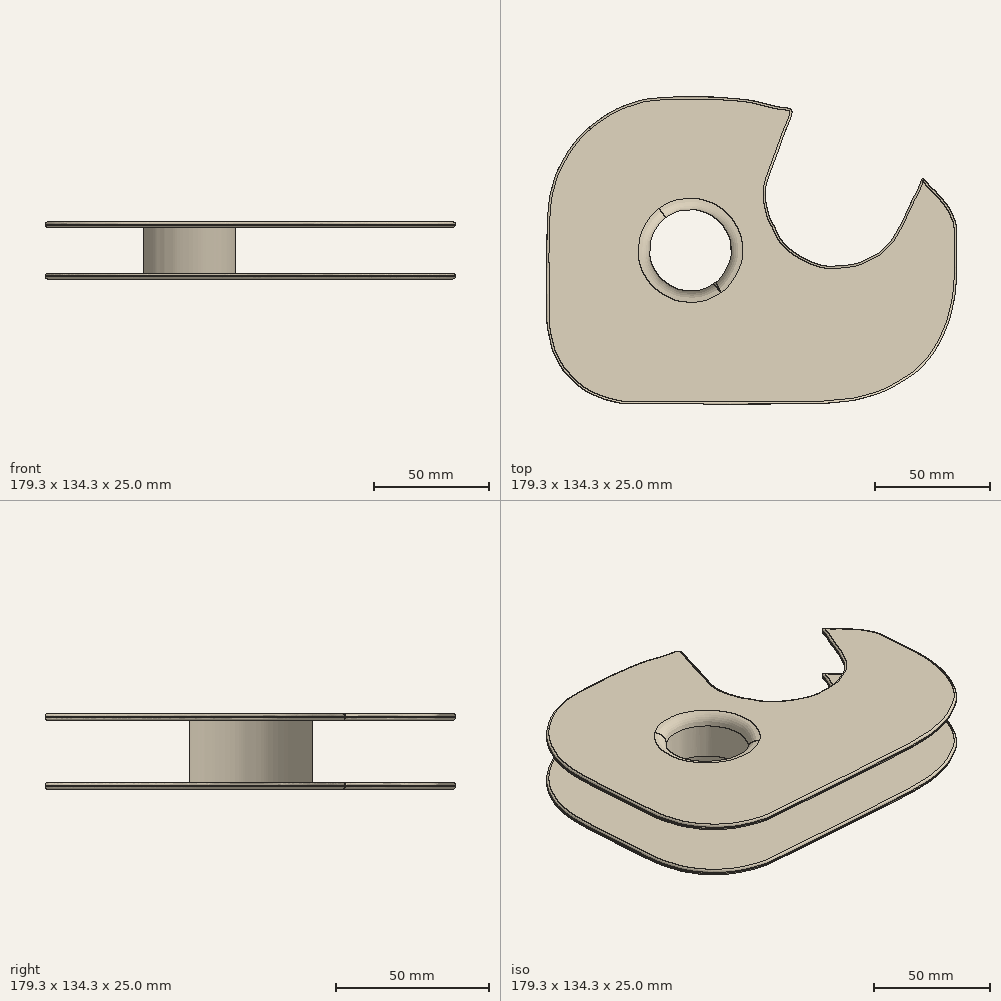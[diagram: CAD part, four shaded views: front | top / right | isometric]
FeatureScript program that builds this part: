
annotation { "Feature Type Name" : "Feature", "Feature Type Description" : "" }
export const myFeature = defineFeature(function(context is Context, id is Id, definition is map)
    precondition{}
    {
        {
            var Q0;
            Q0=qCreatedBy(makeId("Top.planeOp"),FACE);
            var sketch = newSketch(context, id + "F0", { "sketchPlane" : qUnion([Q0])});
            skFitSpline(sketch, "E0", {"points": [v(111.73, 142.36) * mm, v(107.12, 143.84) * mm, v(98.6, 145.82) * mm, v(92.37, 147.1) * mm, v(85.57, 147.8) * mm, v(81.03, 148.1) * mm, v(76.77, 148.37) * mm, v(69.4, 148.37) * mm, v(61.32, 148.37) * mm, v(54.94, 148.1) * mm, v(51.73, 147.73) * mm, v(47.4, 147.28) * mm, v(43.51, 146.14) * mm, v(37.8, 144.2) * mm, v(32.1, 141.34) * mm, v(27.3, 138.14) * mm, v(20.34, 132.32) * mm, v(14.28, 124.9) * mm, v(12, 121.02) * mm, v(8.92, 115.08) * mm, v(7.1, 109.37) * mm, v(5.72, 103.43) * mm, v(5.26, 98.87) * mm, v(4.92, 94.87) * mm, v(4.7, 49.9) * mm, v(4.98, 47.88) * mm, v(5.34, 45.12) * mm, v(6.17, 42) * mm, v(6.63, 39.6) * mm, v(7.55, 36.66) * mm, v(8.7, 34.2) * mm, v(10.18, 31.6) * mm, v(11.5, 29.24) * mm, v(13.73, 26.87) * mm, v(15.5, 24.8) * mm, v(17.28, 23.17) * mm, v(19.36, 21.4) * mm, v(21.28, 20.06) * mm, v(23.65, 18.73) * mm, v(26.76, 17.4) * mm, v(29.57, 16.28) * mm, v(33.28, 15.25) * mm, v(36.68, 14.5) * mm, v(40.38, 14.28) * mm, v(121.15, 14.2) * mm, v(129.89, 14.65) * mm, v(134.18, 15.1) * mm, v(138.92, 15.69) * mm, v(144.99, 17.17) * mm, v(151.2, 19.19) * mm, v(155.79, 21.3) * mm, v(161.76, 24.89) * mm, v(166.55, 28.2) * mm, v(172.43, 34.45) * mm, v(175.65, 39.41) * mm, v(178.22, 44.47) * mm, v(180.43, 49.99) * mm, v(181.53, 53.94) * mm, v(183, 60.84) * mm, v(183.55, 66.08) * mm, v(183.74, 68.65) * mm, v(183.74, 72.14) * mm, v(183.74, 89.98) * mm, v(183.1, 94.3) * mm, v(181.62, 97.61) * mm, v(179.6, 101.2) * mm, v(176.1, 105.33) * mm, v(174.08, 107.54) * mm, v(171.79, 109.75) * mm, v(169.12, 112.5) * mm, v(168.02, 110.67) * mm, v(165.81, 105.7) * mm, v(164.52, 103.5) * mm, v(163.24, 100.46) * mm, v(161.03, 95.77) * mm, v(159.56, 92.65) * mm, v(157.35, 88.97) * mm, v(155.24, 85.38) * mm, v(153.67, 83.82) * mm, v(150.18, 80.33) * mm, v(146.41, 78.4) * mm, v(141.9, 76.1) * mm, v(138.6, 75.18) * mm, v(134.55, 74.63) * mm, v(131.24, 74.44) * mm, v(126.83, 74.44) * mm, v(121.68, 75.73) * mm, v(115.8, 78.49) * mm, v(111.02, 81.8) * mm, v(106.51, 86.76) * mm, v(103.94, 92.1) * mm, v(102.65, 94.3) * mm, v(100.53, 102.02) * mm, v(100.44, 109.01) * mm, v(103.57, 118.57) * mm, v(107.25, 128.32) * mm, v(109.08, 133.65) * mm, v(111.73, 142.36) * mm]});
            skFitSpline(sketch, "E1", {"points": [v(49.78, 78.39) * mm, v(50.73, 74.81) * mm, v(52.22, 72.07) * mm, v(53.65, 70.04) * mm, v(54.85, 68.73) * mm, v(56.34, 67.66) * mm, v(58, 66.35) * mm, v(59.67, 65.51) * mm, v(61.82, 64.44) * mm, v(65.52, 63.72) * mm, v(69.33, 63.6) * mm, v(73.03, 64.26) * mm, v(75.41, 65.4) * mm, v(77.2, 66.35) * mm, v(78.15, 67.06) * mm, v(79.47, 67.78) * mm, v(80.3, 68.8) * mm, v(81.61, 70.46) * mm, v(82.75, 72.3) * mm, v(83.76, 74.28) * mm, v(85.07, 77.85) * mm, v(85.25, 80.65) * mm, v(85.13, 83.58) * mm, v(84.65, 86.26) * mm, v(83.22, 89.48) * mm, v(82.39, 90.85) * mm, v(81.08, 92.82) * mm, v(79.17, 94.66) * mm, v(76.84, 96.4) * mm, v(74.64, 97.52) * mm, v(70.7, 98.84) * mm, v(67.48, 98.96) * mm, v(63.31, 98.6) * mm, v(60.63, 97.76) * mm, v(57.11, 95.74) * mm, v(54.6, 93.53) * mm, v(52.34, 90.43) * mm, v(51.15, 88.28) * mm, v(50.14, 85.18) * mm, v(49.84, 82.14) * mm, v(49.78, 78.39) * mm]});
            skSolve(sketch);
        }
        {
            var Q0;
            Q0 = qSketchRegion(id + "F0", true);
            extrude(context, id + "F1", {"entities" : qUnion([Q0]), "depth" : 25 * mm});
        }
        {
            var Q0;
            Q0=makeQuery(id+"F1.opExtrude","SWEPT_FACE",FACE,{"disambiguationData":[OSD([sQuery(id+"F0.wireOp",EDGE,"E0")])]});
            shell(context, id + "F2", {"entities" : qUnion([Q0]), "thickness" : 2.5 * mm});
        }
        {
            var Q0;
            Q0=makeQuery(id+"F1.opExtrude","CAP_EDGE",EDGE,{"disambiguationData":[OSD([sQuery(id+"F0.wireOp",EDGE,"E1")])],"isStart":false});
            var Q1;
            Q1=makeQuery(id+"F1.opExtrude","CAP_EDGE",EDGE,{"disambiguationData":[OSD([sQuery(id+"F0.wireOp",EDGE,"E1")])],"isStart":true});
            fillet(context, id + "F3", {"entities" : qUnion([Q0, Q1]), "radius" : 5 * mm, "tangentPropagation" : true, "allowEdgeOverflow" : false});
        }
        {
            var Q0;
            Q0=makeQuery(id+"F1.opExtrude","CAP_EDGE",EDGE,{"disambiguationData":[OSD([sQuery(id+"F0.wireOp",EDGE,"E0")])],"isStart":false});
            var Q1;
            {var subQ0=sQuery(id+"F0.wireOp",EDGE,"E0");Q1=makeQuery(id+"F2.opShell","OFFSET_EDGE",EDGE,{"disambiguationData":[OSD([subQ0]),TDD([makeQuery(id+"F1.opExtrude","CAP_EDGE",EDGE,{"disambiguationData":[OSD([subQ0])],"isStart":false})])]});}
            var Q2;
            {var subQ0=sQuery(id+"F0.wireOp",EDGE,"E0");Q2=makeQuery(id+"F2.opShell","OFFSET_EDGE",EDGE,{"disambiguationData":[OSD([subQ0]),TDD([makeQuery(id+"F1.opExtrude","CAP_EDGE",EDGE,{"disambiguationData":[OSD([subQ0])],"isStart":true})])]});}
            var Q3;
            Q3=makeQuery(id+"F1.opExtrude","CAP_EDGE",EDGE,{"disambiguationData":[OSD([sQuery(id+"F0.wireOp",EDGE,"E0")])],"isStart":true});
            fillet(context, id + "F4", {"entities" : qUnion([Q0, Q1, Q2, Q3]), "radius" : 1 * mm, "tangentPropagation" : true, "allowEdgeOverflow" : false});
        }
    });
